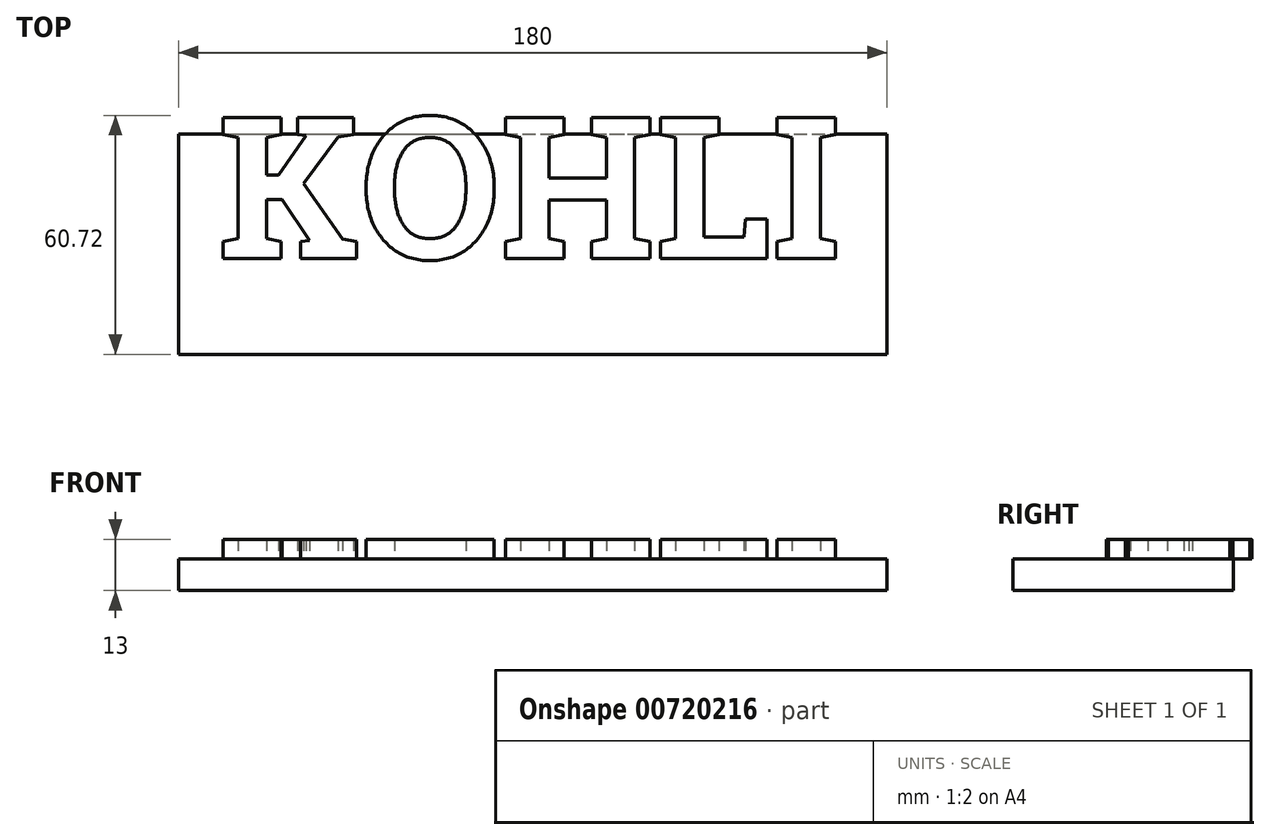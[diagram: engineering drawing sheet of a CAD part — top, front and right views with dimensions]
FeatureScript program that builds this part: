
annotation { "Feature Type Name" : "Feature", "Feature Type Description" : "" }
export const myFeature = defineFeature(function(context is Context, id is Id, definition is map)
    precondition{}
    {
        {
            var Q0;
            Q0=qCreatedBy(makeId("Top.planeOp"),FACE);
            var sketch = newSketch(context, id + "F0", { "sketchPlane" : qUnion([Q0])});
            skLineSegment(sketch, "E0.bottom", {"start": v(-18.04, 6.1) * mm, "end": v(161.96, 6.1) * mm});
            skLineSegment(sketch, "E0.top", {"start": v(-18.04, -49.9) * mm, "end": v(161.96, -49.9) * mm});
            skLineSegment(sketch, "E0.left", {"start": v(-18.04, 6.1) * mm, "end": v(-18.04, -49.9) * mm});
            skLineSegment(sketch, "E0.right", {"start": v(161.96, 6.1) * mm, "end": v(161.96, -49.9) * mm});
            skSolve(sketch);
        }
        {
            var Q0;
            Q0=makeQuery(id+"F0.imprint","IMPRINT",FACE,{"disambiguationData":[TD([[makeQuery(id+"F0.imprint","IMPRINT",EDGE,{"derivedFrom":sQuery(id+"F0.wireOp",EDGE,"E0.bottom")}),-1.0]])]});
            extrude(context, id + "F1", {"entities" : qUnion([Q0]), "depth" : 8 * mm, "offsetDistance" : 25.4 * mm});
        }
        {
            var Q0;
            Q0=makeQuery(id+"F1.opExtrude","CAP_FACE",FACE,{"disambiguationData":[OSD([sQuery(id+"F0.wireOp",EDGE,"E0.bottom"),sQuery(id+"F0.wireOp",EDGE,"E0.top"),sQuery(id+"F0.wireOp",EDGE,"E0.left"),sQuery(id+"F0.wireOp",EDGE,"E0.right")])],"isStart":false});
            var sketch = newSketch(context, id + "F2", { "sketchPlane" : qUnion([Q0])});
            skText(sketch, "E1", { "text": "KOHLI", "fontName": "RobotoSlab-Bold.ttf"});
            skLineSegment(sketch, "E2", {"start": v(161.96, -49.9) * mm, "end": v(161.96, 6.1) * mm});
            skLineSegment(sketch, "E3", {"start": v(71.96, 6.1) * mm, "end": v(71.96, -49.9) * mm, "construction": true});
            skLineSegment(sketch, "E4", {"start": v(-18.04, -21.9) * mm, "end": v(161.96, -21.9) * mm, "construction": true});
            const initialGuessF2  = {"E1": [-0.00804, -0.02556, 1, 0, 0.03632]};
            skSetInitialGuess(sketch, initialGuessF2);
            skSolve(sketch);
        }
        {
            var Q0;
            Q0 = qSketchRegion(id + "F2", true);
            extrude(context, id + "F3", {"entities" : qUnion([Q0]), "operationType" : NewBodyOperationType.ADD, "depth" : 5 * mm, "offsetDistance" : 25.4 * mm});
        }
    });
